# Revit family: v-316_317k7_kr7_kp7_50Hz
name_source: partatom
category: 機械設備
units: mm (PartAtom-declared; Revit-internal decimal feet)

## family parameters
OmniClass タイトル = Centrifugal Fans
OmniClass 番号 = 23.75.35.17.27
パーツ タイプ = 標準
ロード時にボイドで切り取り = いいえ
丸型コネクタ寸法 = 直径を使用
作業面ベース = いいえ
共有 = いいえ
常に垂直 = はい
部屋計算ポイント = いいえ

## types (4) — shared parameters
D1 = 95
Depth = 580  [stored 1.90289 ft]
Duct_D = 178  [stored 0.58399 ft]
Duct_H = 91  [stored 0.298556 ft]
Duct_Height = 46  [stored 0.150919 ft]
Duct_W = 210  [stored 0.688976 ft]
EAサイズ_D = 291  [stored 0.954724 ft]
EAサイズ_W = 102
EAダクト接続口_上部右 = はい
EAダクト接続口_上部左 = いいえ
EAダクト接続口_右 = いいえ
EAダクト接続口_左 = いいえ
EAダクト接続口_後部 = いいえ
H1 = 110  [stored 0.360892 ft]
Height = 190
IfcExportAs = IfcFanType
IfcExportType = CENTRIFUGALFORWARDCURVED
MAX静圧 = 0.0 Pa
MID静圧 = 0.0 Pa
MIN静圧 = 0.0 Pa
OmniClassCode = 23-33 31 19 13 15
URL = https://www.mitsubishielectric.co.jp
Uniclass2015Code = Pr_65_67_29_12
Uniclass2015Title = Centrifugal fans
Uniclass2015Version = Systems v1.9
☑給気／□排気 = いいえ
ダクト幅 = 102 mm
ダクト高 = 291 mm
マテリアル = 鋼板(白)
仕様書バージョン = Version1.0
企業コード = 108420
分類コード = 50052503100060
取付金具_Depth = 6  [stored 0.019685 ft]
取付金具_H = 30  [stored 0.0984252 ft]
取付金具_径 = 10  [stored 0.0328084 ft]
取付金具_穴位置 = 16  [stored 0.0524934 ft]
周波数 = 50 Hz
呼称 = 遠心送風機
外気量 = 0.0 m³/h
天吊用穴_D1 = 15  [stored 0.0492126 ft]
天吊用穴_D2 = 336  [stored 1.10236 ft]
天吊用穴_ピッチ = 250  [stored 0.82021 ft]
実風量 = 0.0 m³/h
形式 = 片吸込形
排気量 = 0.0 m³/h
極数 = 2
機外静圧 = 0.0 Pa
機外静圧_排気 = 210.0 Pa
法定耐用年数 = 15
相 = 1
積算_科目 = 2 換気設備
符号 = FE
製品リリース年月 = 2022年6月1日
製品出荷対象 = 国内
製造元 = 三菱電機株式会社
設置方法 = 天吊
設計風量 = 0.0 m³/h
説明 = レンジフードファン 浅形 標準タイプ
負荷分類 = 3_ファン類
運転質量 = 0.00 kg
電動機出力 = 0 W
電圧 = 100 V
zero-valued in all types: Clearance Back, Clearance Bottom, Clearance Front, Clearance Left, Clearance Right, Clearance Top

## per-type parameters (varying)
| type | MAX風量 | MID風量 | MIN風量 | W1 | Width | 価格 | 取付金具_ピッチ | 消費電力 | 製品質量 | 質量 | 風量 | 騒音レベル(dB(A)) |
| V-316K7 | 590.0 m³/h | 0.0 m³/h | 360.0 m³/h | 300  [stored 0.984252 ft] | 600  [stored 1.9685 ft] | 61700 $ | 500  [stored 1.64042 ft] | 72 W | 12.00 kg | 14.40 kg | 590.0 m³/h | 46.5 |
| V-316KR7 | 590.0 m³/h | 0.0 m³/h | 360.0 m³/h | 300  [stored 0.984252 ft] | 600  [stored 1.9685 ft] | 72500 $ | 500  [stored 1.64042 ft] | 72 W | 12.00 kg | 14.40 kg | 590.0 m³/h | 46.5 |
| V-316KP7 | 755.0 m³/h | 610.0 m³/h | 375.0 m³/h | 300  [stored 0.984252 ft] | 600  [stored 1.9685 ft] | 64800 $ | 500  [stored 1.64042 ft] | 99 W | 13.00 kg | 15.60 kg | 755.0 m³/h | 52.5 |
| V-317K7 | 590.0 m³/h | 0.0 m³/h | 360.0 m³/h | 350  [stored 1.14829 ft] | 700  [stored 2.29659 ft] | 64200 $ | 600  [stored 1.9685 ft] | 72 W | 13.00 kg | 15.60 kg | 590.0 m³/h | 46.5 |

note: column(s) folded — value = type name in every type: モデル

note: [stored X ft] marks values corroborated as IEEE doubles in the binary element streams (Revit-internal decimal feet)
